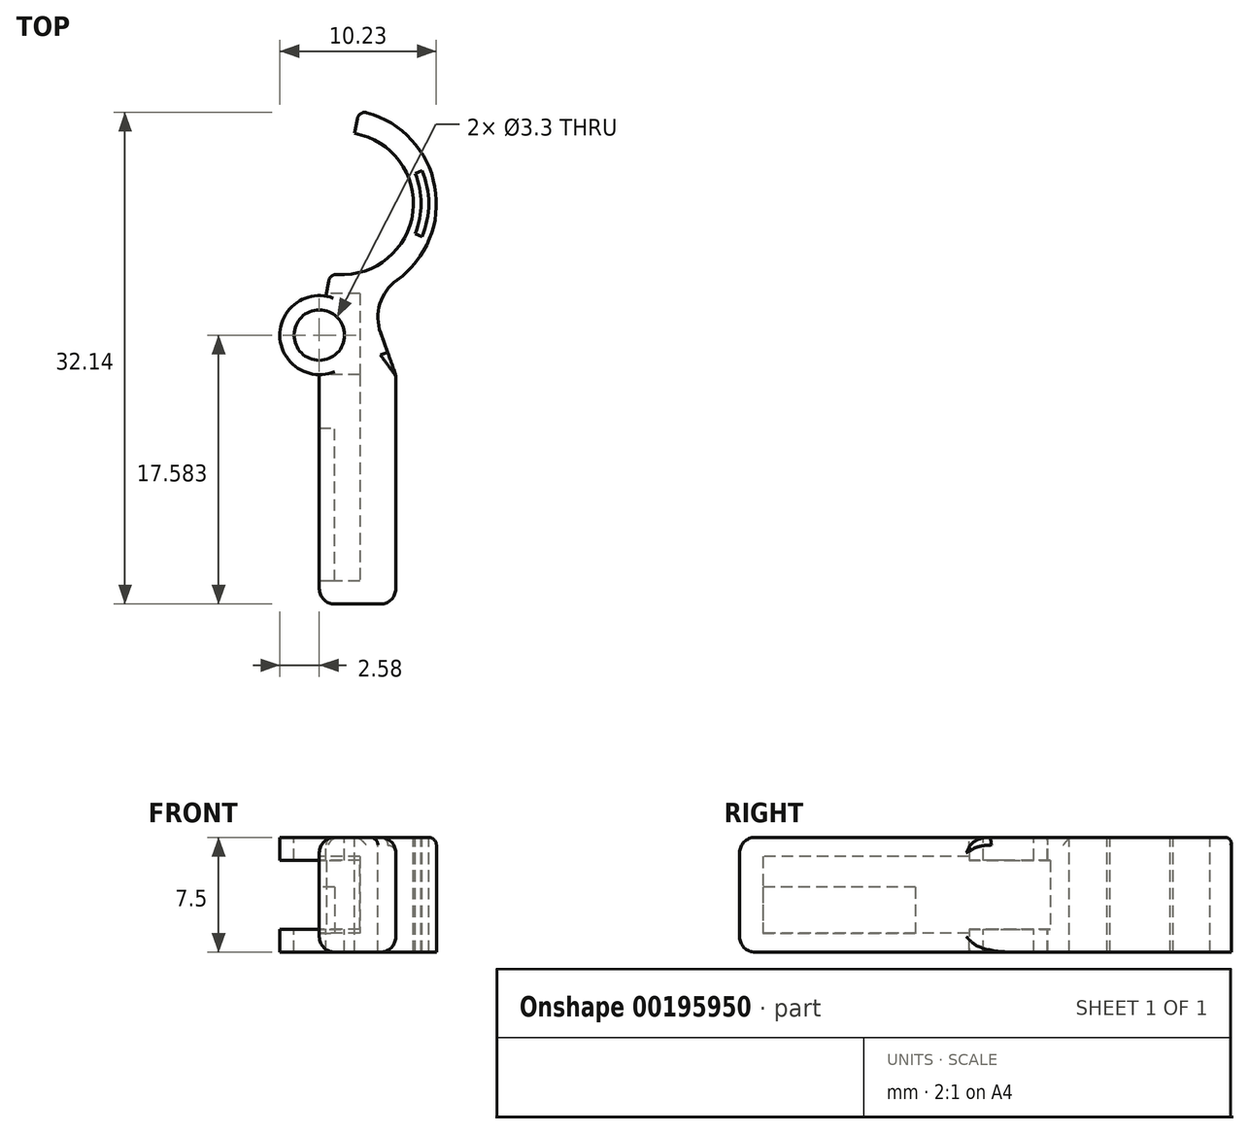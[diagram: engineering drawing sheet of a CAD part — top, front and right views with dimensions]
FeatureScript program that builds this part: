
annotation { "Feature Type Name" : "Feature", "Feature Type Description" : "" }
export const myFeature = defineFeature(function(context is Context, id is Id, definition is map)
    precondition{}
    {
        {
            var Q0;
            Q0=qCreatedBy(makeId("Front.planeOp"),FACE);
            var sketch = newSketch(context, id + "F0", { "sketchPlane" : qUnion([Q0])});
            skLineSegment(sketch, "E0.bottom", {"start": v(-2.5, 3.75) * mm, "end": v(2.5, 3.75) * mm});
            skLineSegment(sketch, "E0.top", {"start": v(-2.5, -3.75) * mm, "end": v(2.5, -3.75) * mm});
            skLineSegment(sketch, "E0.left", {"start": v(-2.5, 3.75) * mm, "end": v(-2.5, -3.75) * mm});
            skLineSegment(sketch, "E0.right", {"start": v(2.5, 3.75) * mm, "end": v(2.5, -3.75) * mm});
            skSolve(sketch);
        }
        {
            var Q0;
            Q0=makeQuery(id+"F0.imprint","IMPRINT",FACE,{"disambiguationData":[TD([[makeQuery(id+"F0.imprint","IMPRINT",EDGE,{"derivedFrom":sQuery(id+"F0.wireOp",EDGE,"E0.bottom")}),-1.0]])]});
            extrude(context, id + "F1", {"entities" : qUnion([Q0]), "oppositeDirection" : true, "depth" : 15 * mm});
        }
        {
            var Q0;
            Q0=makeQuery(id+"F1.opExtrude","SWEPT_FACE",FACE,{"disambiguationData":[OSD([sQuery(id+"F0.wireOp",EDGE,"E0.bottom")])]});
            var sketch = newSketch(context, id + "F2", { "sketchPlane" : qUnion([Q0])});
            skLineSegment(sketch, "E1", {"start": v(2.5, 15) * mm, "end": v(-2.5, 15) * mm});
            skCircle(sketch, "E2", {"center": v(-2.5, 17.58) * mm, "radius": 1.65 * mm});
            skLineSegment(sketch, "E3", {"start": v(-2.5, 32.47) * mm, "end": v(-2.5, 20.17) * mm, "construction": true});
            skLineSegment(sketch, "E4", {"start": v(2.5, 15) * mm, "end": v(0.6, 20.24) * mm});
            skArc(sketch, "E5", {"start": v(-2.5, 20.17) * mm, "mid": v(-5.08, 17.58) * mm, "end": v(-2.5, 15) * mm});
            skLineSegment(sketch, "E6.trimOffspring", {"start": v(-0.19, 30.76) * mm, "end": v(0.07, 32.24) * mm});
            skArc(sketch, "E7", {"start": v(-2.06, 20.13) * mm, "mid": v(-5.07, 17.8) * mm, "end": v(-2.5, 15) * mm});
            skLineSegment(sketch, "E8.trimOffspring", {"start": v(-2.06, 20.13) * mm, "end": v(-1.8, 21.6) * mm});
            skLineSegment(sketch, "E9", {"start": v(-0.27, 30.27) * mm, "end": v(-1.72, 22.1) * mm, "construction": true});
            skPoint(sketch, "E10", {"position": v(-1, 26.18) * mm});
            skArc(sketch, "E11", {"start": v(-2.5, 20.22) * mm, "mid": v(-2.28, 20.17) * mm, "end": v(-2.06, 20.13) * mm});
            skArc(sketch, "E12.trimOffspring", {"start": v(0.6, 20.24) * mm, "mid": v(5.15, 26.45) * mm, "end": v(0.07, 32.24) * mm});
            skArc(sketch, "E13", {"start": v(-1.8, 21.6) * mm, "mid": v(3.58, 25.38) * mm, "end": v(-0.19, 30.76) * mm});
            skSolve(sketch);
        }
        {
            var Q0;
            Q0=qSketchRegion(id+"F2",true);
            var Q1;
            Q1=makeQuery(id+"F1.opExtrude","SWEPT_FACE",FACE,{"disambiguationData":[OSD([sQuery(id+"F0.wireOp",EDGE,"E0.top")])]});
            extrude(context, id + "F3", {"entities" : qUnion([Q0]), "operationType" : NewBodyOperationType.ADD, "endBound" : BoundingType.UP_TO_SURFACE, "oppositeDirection" : true, "endBoundEntityFace" : qUnion([Q1]), "depth" : 25 * mm});
        }
        {
            var Q0;
            Q0=makeQuery(id+"F3.boolean.opBoolean","MERGE",FACE,{"derivedFrom":[makeQuery(id+"F1.opExtrude","SWEPT_FACE",FACE,{"disambiguationData":[OSD([sQuery(id+"F0.wireOp",EDGE,"E0.bottom")])]}),makeQuery(id+"F3.opExtrude","CAP_FACE",FACE,{"disambiguationData":[OSD([sQuery(id+"F2.wireOp",EDGE,"E1"),sQuery(id+"F2.wireOp",EDGE,"E2"),sQuery(id+"F2.wireOp",EDGE,"B9JCAYym-b5s2-WaWf-YfGt-LBT5zxrqjMaR"),sQuery(id+"F2.wireOp",EDGE,"Ub5ObEa3-LSRd-y38C-kyzX-ncU0hSC1jkLU"),sQuery(id+"F2.wireOp",EDGE,"msjFJeTt-mXro-ggz3-w7Y5-5ResKncMShYH"),sQuery(id+"F2.wireOp",EDGE,"pVOFhWqQ-R0tv-80Kr-So2p-xKMuH6NPngEm"),sQuery(id+"F2.wireOp",EDGE,"6c9f61bb-61ba-4d6e-9064-ecf24c568932.trimOffspring"),sQuery(id+"F2.wireOp",EDGE,"f9b7a8c3-8cce-441f-8e96-de4bfab7fc40.trimOffspring"),sQuery(id+"F2.wireOp",EDGE,"E4")])],"isStart":true})]});
            var sketch = newSketch(context, id + "F4", { "sketchPlane" : qUnion([Q0])});
            skPoint(sketch, "E14", {"position": v(-2.5, 17.65) * mm});
            skLineSegment(sketch, "E15", {"start": v(-5.15, 17.65) * mm, "end": v(-5.15, 15.22) * mm, "construction": true});
            skSolve(sketch);
        }
        {
            var Q0;
            Q0=sQuery(id+"F4.wireOp",EDGE,"E15");
            cPlane(context, id + "F5", {"entities" : qUnion([Q0]), "cplaneType" : CPlaneType.LINE_ANGLE, "offset" : 25 * mm, "angle" : 90 * degree, "width" : 150 * mm, "height" : 150 * mm});
        }
        {
            var Q0;
            Q0=qCreatedBy(id+"F5.planeOp",FACE);
            var sketch = newSketch(context, id + "F6", { "sketchPlane" : qUnion([Q0])});
            skLineSegment(sketch, "E16.left", {"start": v(20.3, -2.25) * mm, "end": v(20.3, 2.25) * mm});
            skLineSegment(sketch, "E17", {"start": v(20.3, 2.25) * mm, "end": v(15, 2.25) * mm});
            skLineSegment(sketch, "E18", {"start": v(20.3, -2.25) * mm, "end": v(15, -2.25) * mm});
            skLineSegment(sketch, "E19.bottom", {"start": v(15, 2.5) * mm, "end": v(1.5, 2.5) * mm});
            skLineSegment(sketch, "E19.top", {"start": v(15, -2.5) * mm, "end": v(1.5, -2.5) * mm});
            skLineSegment(sketch, "E19.left", {"start": v(15, 2.5) * mm, "end": v(15, 2.25) * mm});
            skLineSegment(sketch, "E19.right", {"start": v(1.5, 2.5) * mm, "end": v(1.5, -2.5) * mm});
            skLineSegment(sketch, "E20.trimOffspring", {"start": v(15, -2.25) * mm, "end": v(15, -2.5) * mm});
            skSolve(sketch);
        }
        {
            var Q0;
            Q0=qSketchRegion(id+"F6",true);
            extrude(context, id + "F7", {"entities" : qUnion([Q0]), "operationType" : NewBodyOperationType.REMOVE, "depth" : 5.3 * mm});
        }
        {
            var Q0;
            {var subQ0=sQuery(id+"F0.wireOp",EDGE,"E0.bottom");Q0=makeQuery(id+"F4.imprint","IMPRINT",FACE,{"disambiguationData":[TD([[makeQuery(id+"F4.imprint","IMPRINT",EDGE,{"derivedFrom":makeQuery(id+"F1.opExtrude","CAP_EDGE",EDGE,{"disambiguationData":[OSD([subQ0])],"isStart":true})}),1.0]])]});}
            var sketch = newSketch(context, id + "F8", { "sketchPlane" : qUnion([Q0])});
            skPoint(sketch, "E21.orphan", {"position": v(-1.9, 31.06) * mm});
            skPoint(sketch, "E22.orphan", {"position": v(-1.7, 32.55) * mm});
            skPoint(sketch, "E23.orphan", {"position": v(-3.1, 21.84) * mm});
            skPoint(sketch, "E24.orphan", {"position": v(0.32, 20.99) * mm});
            skPoint(sketch, "E25.orphan", {"position": v(0.07, 32.24) * mm});
            skPoint(sketch, "E26.0.start.orphan", {"position": v(0.6, 20.24) * mm});
            skArc(sketch, "E27.0", {"start": v(4.22, 24.02) * mm, "mid": v(4.65, 26.18) * mm, "end": v(4.22, 28.35) * mm});
            skArc(sketch, "E28.0", {"start": v(3.76, 24.21) * mm, "mid": v(4.15, 26.18) * mm, "end": v(3.76, 28.16) * mm});
            skLineSegment(sketch, "E29", {"start": v(3.76, 28.16) * mm, "end": v(4.22, 28.35) * mm});
            skLineSegment(sketch, "E30", {"start": v(3.76, 24.21) * mm, "end": v(4.22, 24.02) * mm});
            skLineSegment(sketch, "E31", {"start": v(-1, 26.18) * mm, "end": v(7.11, 26.18) * mm, "construction": true});
            skSolve(sketch);
        }
        {
            var Q0;
            Q0=qSketchRegion(id+"F8",true);
            extrude(context, id + "F9", {"entities" : qUnion([Q0]), "operationType" : NewBodyOperationType.REMOVE, "endBound" : BoundingType.THROUGH_ALL, "oppositeDirection" : true, "depth" : 25 * mm});
        }
        {
            var Q0;
            Q0=makeQuery(id+"F3.opExtrude","SWEPT_EDGE",EDGE,{"disambiguationData":[OSD([sQuery(id+"F2.wireOp",EDGE,"E4"),sQuery(id+"F2.wireOp",EDGE,"K92U0NBN-zdy9-IzVP-x1tL-mb1lYgoXCjgz")])]});
            fillet(context, id + "F10", {"entities" : qUnion([Q0]), "radius" : 3 * mm, "tangentPropagation" : true, "allowEdgeOverflow" : false});
        }
        {
            var Q0;
            Q0=makeQuery(id+"F7.boolean.opBoolean","COPY",FACE,{"derivedFrom":makeQuery(id+"F7.opExtrude","SWEPT_FACE",FACE,{"disambiguationData":[OSD([sQuery(id+"F6.wireOp",EDGE,"E19.top")])]})});
            var sketch = newSketch(context, id + "F11", { "sketchPlane" : qUnion([Q0])});
            skLineSegment(sketch, "E32.bottom", {"start": v(-2.5, 1.5) * mm, "end": v(-1.5, 1.5) * mm});
            skLineSegment(sketch, "E32.top", {"start": v(-2.5, 11.5) * mm, "end": v(-1.5, 11.5) * mm});
            skLineSegment(sketch, "E32.left", {"start": v(-2.5, 1.5) * mm, "end": v(-2.5, 11.5) * mm});
            skLineSegment(sketch, "E32.right", {"start": v(-1.5, 1.5) * mm, "end": v(-1.5, 11.5) * mm});
            skSolve(sketch);
        }
        {
            var Q0;
            Q0 = qSketchRegion(id + "F11", true);
            extrude(context, id + "F12", {"entities" : qUnion([Q0]), "operationType" : NewBodyOperationType.ADD, "depth" : 3 * mm});
        }
        {
            var Q0;
            Q0=makeQuery(id+"F1.opExtrude","SWEPT_FACE",FACE,{"disambiguationData":[OSD([sQuery(id+"F0.wireOp",EDGE,"E0.right")])]});
            var Q1;
            Q1=makeQuery(id+"F1.opExtrude","CAP_FACE",FACE,{"disambiguationData":[OSD([sQuery(id+"F0.wireOp",EDGE,"E0.bottom"),sQuery(id+"F0.wireOp",EDGE,"E0.top"),sQuery(id+"F0.wireOp",EDGE,"E0.left"),sQuery(id+"F0.wireOp",EDGE,"E0.right")])],"isStart":true});
            var Q2;
            Q2=makeQuery(id+"F1.opExtrude","SWEPT_EDGE",EDGE,{"disambiguationData":[OSD([sQuery(id+"F0.wireOp",EDGE,"E0.top"),sQuery(id+"F0.wireOp",EDGE,"E0.left")])]});
            var Q3;
            Q3=makeQuery(id+"F1.opExtrude","SWEPT_EDGE",EDGE,{"disambiguationData":[OSD([sQuery(id+"F0.wireOp",EDGE,"E0.bottom"),sQuery(id+"F0.wireOp",EDGE,"E0.left")])]});
            fillet(context, id + "F13", {"entities" : qUnion([Q0, Q1, Q2, Q3]), "radius" : 1 * mm, "tangentPropagation" : true, "allowEdgeOverflow" : false});
        }
        {
            var Q0;
            Q0=makeQuery(id+"F3.opExtrude","CAP_EDGE",EDGE,{"disambiguationData":[OSD([sQuery(id+"F2.wireOp",EDGE,"E12.trimOffspring")])],"isStart":true});
            var Q1;
            Q1=makeQuery(id+"F3.opExtrude","CAP_EDGE",EDGE,{"disambiguationData":[OSD([sQuery(id+"F2.wireOp",EDGE,"E8.trimOffspring")])],"isStart":true});
            var Q2;
            Q2=makeQuery(id+"F3.opExtrude","SWEPT_EDGE",EDGE,{"disambiguationData":[OSD([sQuery(id+"F2.wireOp",EDGE,"E8.trimOffspring"),sQuery(id+"F2.wireOp",EDGE,"E13")])]});
            var Q3;
            Q3=makeQuery(id+"F3.opExtrude","SWEPT_EDGE",EDGE,{"disambiguationData":[OSD([sQuery(id+"F2.wireOp",EDGE,"E6.trimOffspring"),sQuery(id+"F2.wireOp",EDGE,"E12.trimOffspring")])]});
            var Q4;
            Q4=makeQuery(id+"F3.opExtrude","TWEAK_EDGE",EDGE,{"derivedFrom":[makeQuery(id+"F1.opExtrude","SWEPT_FACE",FACE,{"disambiguationData":[OSD([sQuery(id+"F0.wireOp",EDGE,"E0.top")])]}),makeQuery(id+"F2.imprint","IMPRINT",EDGE,{"derivedFrom":sQuery(id+"F2.wireOp",EDGE,"E8.trimOffspring")})]});
            var Q5;
            Q5=makeQuery(id+"F3.opExtrude","TWEAK_EDGE",EDGE,{"derivedFrom":[makeQuery(id+"F1.opExtrude","SWEPT_FACE",FACE,{"disambiguationData":[OSD([sQuery(id+"F0.wireOp",EDGE,"E0.top")])]}),makeQuery(id+"F2.imprint","IMPRINT",EDGE,{"derivedFrom":sQuery(id+"F2.wireOp",EDGE,"E12.trimOffspring")})]});
            fillet(context, id + "F14", {"entities" : qUnion([Q0, Q1, Q2, Q3, Q4, Q5]), "radius" : .5 * mm, "tangentPropagation" : true, "allowEdgeOverflow" : false});
        }
    });
